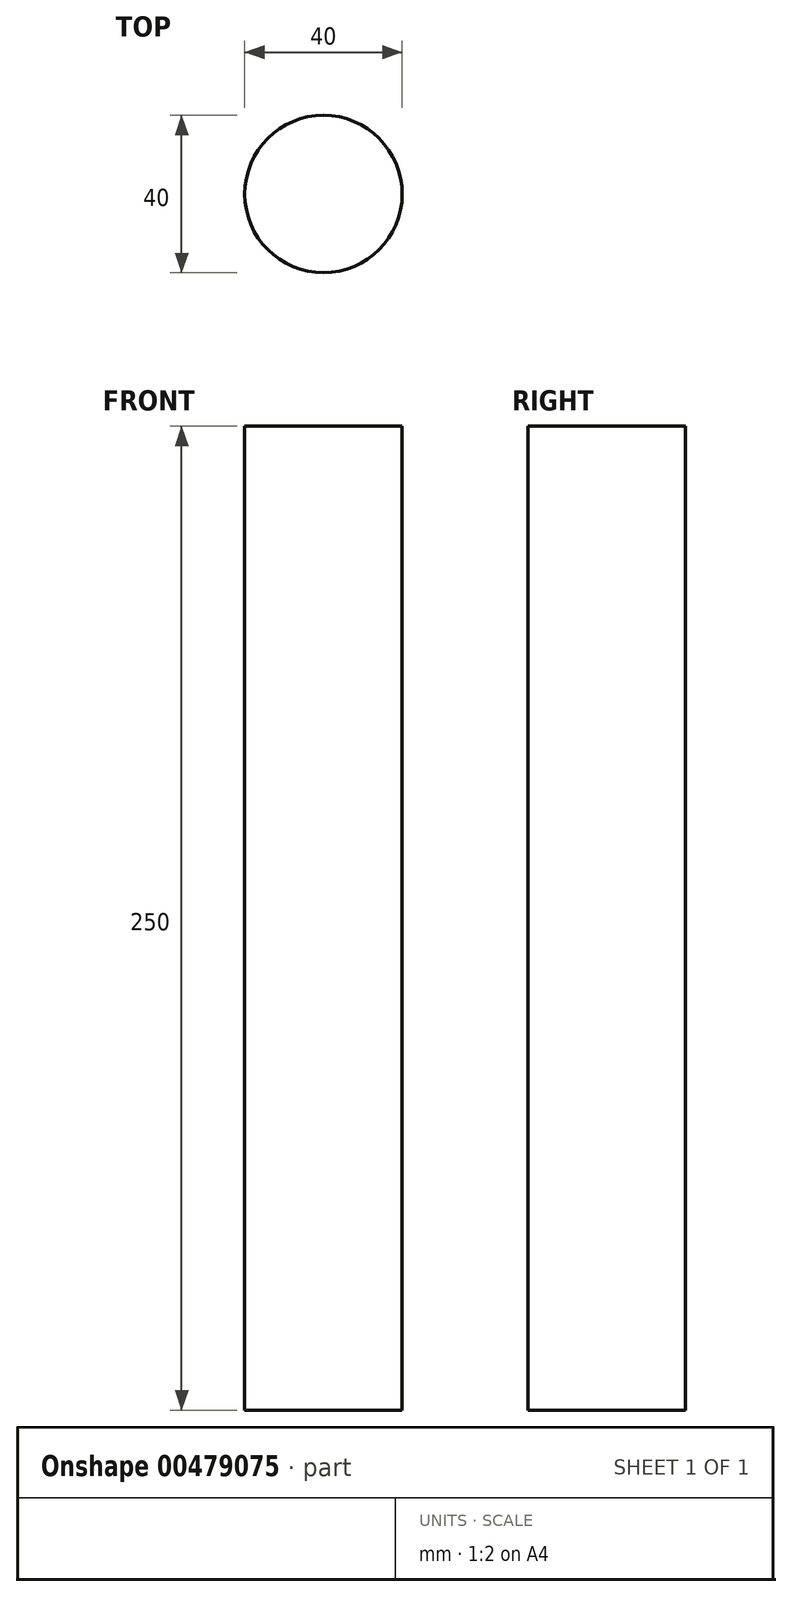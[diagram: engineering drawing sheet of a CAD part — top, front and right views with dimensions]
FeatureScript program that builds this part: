
annotation { "Feature Type Name" : "Feature", "Feature Type Description" : "" }
export const myFeature = defineFeature(function(context is Context, id is Id, definition is map)
    precondition{}
    {
        {
            var Q0;
            Q0=qCreatedBy(makeId("Top.planeOp"),FACE);
            var sketch = newSketch(context, id + "F0", { "sketchPlane" : qUnion([Q0])});
            skCircle(sketch, "E0", {"center": v(0, 0) * mm, "radius": 20 * mm});
            skSolve(sketch);
        }
        {
            var Q0;
            Q0=makeQuery(id+"F0.imprint","IMPRINT",FACE,{"disambiguationData":[TD([[makeQuery(id+"F0.imprint","IMPRINT",EDGE,{"derivedFrom":sQuery(id+"F0.wireOp",EDGE,"E0")}),1.0]])]});
            extrude(context, id + "F1", {"entities" : qUnion([Q0]), "depth" : 200 * mm, "hasSecondDirection" : true, "secondDirectionOppositeDirection" : true, "secondDirectionDepth" : 50 * mm});
        }
    });
